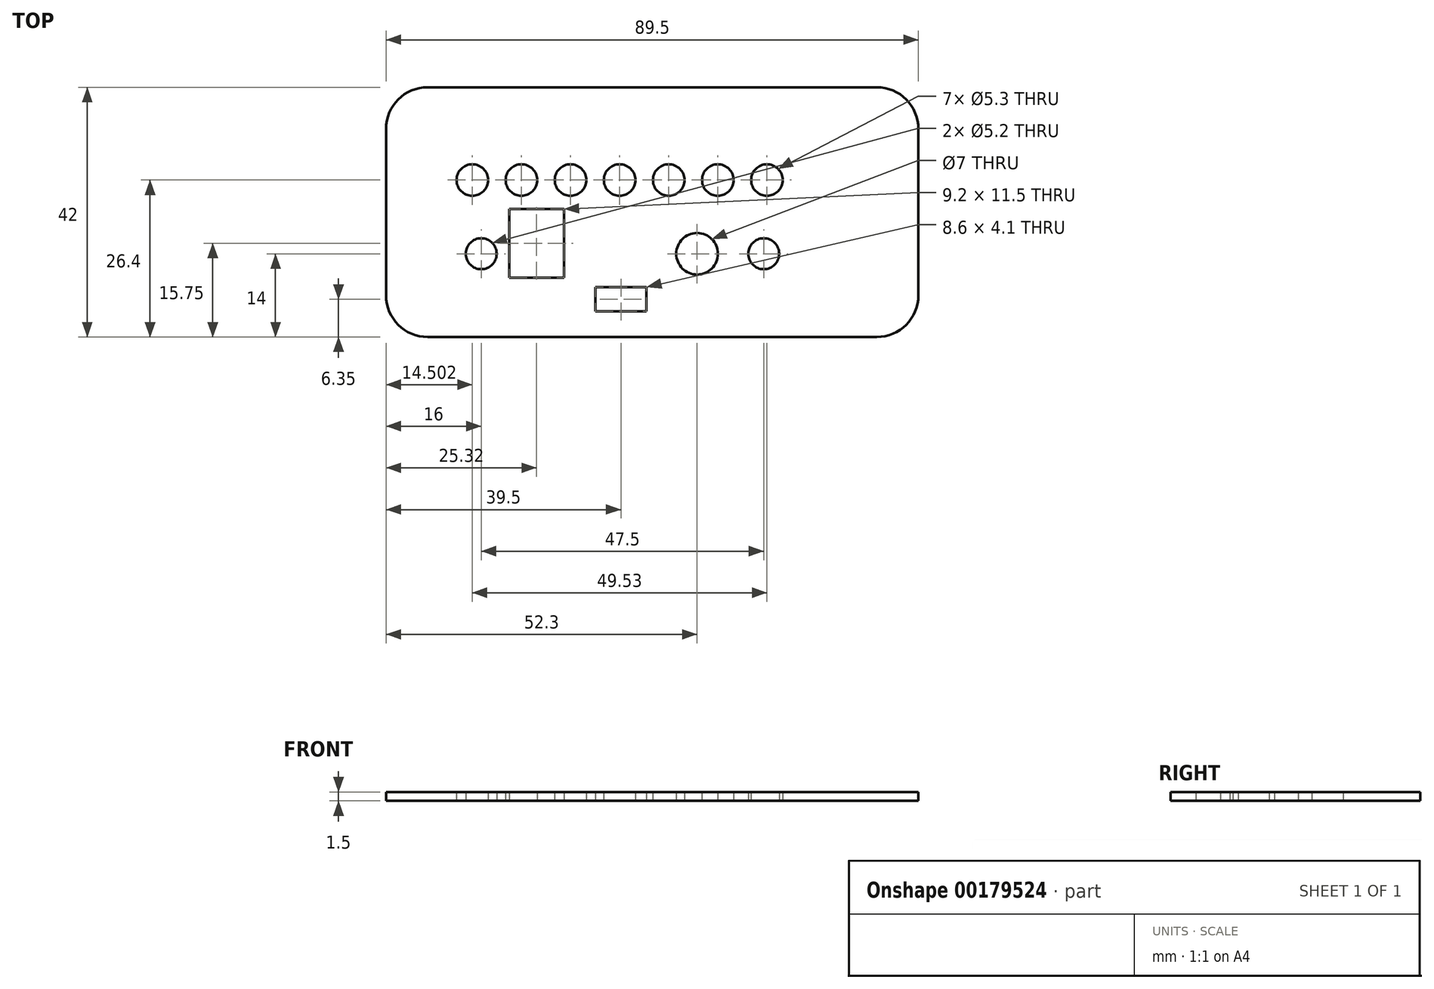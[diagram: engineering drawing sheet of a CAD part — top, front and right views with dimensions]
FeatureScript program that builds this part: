
annotation { "Feature Type Name" : "Feature", "Feature Type Description" : "" }
export const myFeature = defineFeature(function(context is Context, id is Id, definition is map)
    precondition{}
    {
        {
            var Q0;
            Q0=qCreatedBy(makeId("Top.planeOp"),FACE);
            var sketch = newSketch(context, id + "F0", { "sketchPlane" : qUnion([Q0])});
            skLineSegment(sketch, "E0.bottom", {"start": v(37.75, -21) * mm, "end": v(-37.75, -21) * mm});
            skLineSegment(sketch, "E0.top", {"start": v(37.75, 21) * mm, "end": v(-37.75, 21) * mm});
            skLineSegment(sketch, "E0.left", {"start": v(44.75, -14) * mm, "end": v(44.75, 14) * mm});
            skLineSegment(sketch, "E0.right", {"start": v(-44.75, -14) * mm, "end": v(-44.75, 14) * mm});
            skPoint(sketch, "E0.middle", {"position": v(0, 0) * mm});
            skPoint(sketch, "E1.visualSharp", {"position": v(-44.75, 21) * mm});
            skArc(sketch, "E1.filletArc", {"start": v(-37.75, 21) * mm, "mid": v(-42.7, 18.95) * mm, "end": v(-44.75, 14) * mm});
            skPoint(sketch, "E2.visualSharp", {"position": v(-44.75, -21) * mm});
            skArc(sketch, "E2.filletArc", {"start": v(-44.75, -14) * mm, "mid": v(-42.7, -18.95) * mm, "end": v(-37.75, -21) * mm});
            skPoint(sketch, "E3.visualSharp", {"position": v(44.75, 21) * mm});
            skArc(sketch, "E3.filletArc", {"start": v(44.75, 14) * mm, "mid": v(42.7, 18.95) * mm, "end": v(37.75, 21) * mm});
            skPoint(sketch, "E4.visualSharp", {"position": v(44.75, -21) * mm});
            skArc(sketch, "E4.filletArc", {"start": v(37.75, -21) * mm, "mid": v(42.7, -18.95) * mm, "end": v(44.75, -14) * mm});
            skLineSegment(sketch, "E5.bottom", {"start": v(-9.55, -12.6) * mm, "end": v(-0.95, -12.6) * mm});
            skLineSegment(sketch, "E5.top", {"start": v(-9.55, -16.7) * mm, "end": v(-0.95, -16.7) * mm});
            skLineSegment(sketch, "E5.left", {"start": v(-9.55, -12.6) * mm, "end": v(-9.55, -16.7) * mm});
            skLineSegment(sketch, "E5.right", {"start": v(-0.95, -12.6) * mm, "end": v(-0.95, -16.7) * mm});
            skPoint(sketch, "E6", {"position": v(7.55, -7) * mm});
            skPoint(sketch, "E7", {"position": v(18.75, -7) * mm});
            skPoint(sketch, "E8", {"position": v(-28.75, -7) * mm});
            skLineSegment(sketch, "E9.bottom", {"start": v(-24.03, 0.5) * mm, "end": v(-14.83, 0.5) * mm});
            skLineSegment(sketch, "E9.top", {"start": v(-24.03, -11) * mm, "end": v(-14.83, -11) * mm});
            skLineSegment(sketch, "E9.left", {"start": v(-24.03, 0.5) * mm, "end": v(-24.03, -11) * mm});
            skLineSegment(sketch, "E9.right", {"start": v(-14.83, 0.5) * mm, "end": v(-14.83, -11) * mm});
            skPoint(sketch, "E10", {"position": v(-30.25, 5.4) * mm});
            skPoint(sketch, "E11.1.0.0", {"position": v(-22, 5.4) * mm});
            skPoint(sketch, "E11.2.0.0", {"position": v(-13.74, 5.4) * mm});
            skPoint(sketch, "E11.3.0.0", {"position": v(-5.48, 5.4) * mm});
            skPoint(sketch, "E11.4.0.0", {"position": v(2.77, 5.4) * mm});
            skPoint(sketch, "E11.5.0.0", {"position": v(11.03, 5.4) * mm});
            skPoint(sketch, "E11.6.0.0", {"position": v(19.28, 5.4) * mm});
            skLineSegment(sketch, "E11.direction1", {"start": v(-30.25, 5.4) * mm, "end": v(-22, 5.4) * mm, "construction": true});
            skLineSegment(sketch, "E11.direction2", {"start": v(-30.25, 5.4) * mm, "end": v(-30.25, 15.4) * mm, "construction": true});
            skSolve(sketch);
        }
        {
            var Q0;
            Q0=makeQuery(id+"F0.imprint","IMPRINT",FACE,{"disambiguationData":[TD([[makeQuery(id+"F0.imprint","IMPRINT",EDGE,{"derivedFrom":sQuery(id+"F0.wireOp",EDGE,"E0.bottom")}),-1.0]])]});
            extrude(context, id + "F1", {"entities" : qUnion([Q0]), "depth" : 1.5 * mm});
        }
        {
            var Q0;
            Q0=sQuery(id+"F0.wireOp",VERTEX,"E7");
            var Q1;
            Q1=sQuery(id+"F0.wireOp",VERTEX,"E8");
            var Q2;
            Q2=makeQuery(id+"F1.opExtrude","SWEPT_BODY",BODY,{"disambiguationData":[OSD([sQuery(id+"F0.wireOp",EDGE,"E0.bottom"),sQuery(id+"F0.wireOp",EDGE,"E0.top"),sQuery(id+"F0.wireOp",EDGE,"E0.left"),sQuery(id+"F0.wireOp",EDGE,"E0.right"),sQuery(id+"F0.wireOp",EDGE,"E1.filletArc"),sQuery(id+"F0.wireOp",EDGE,"E2.filletArc"),sQuery(id+"F0.wireOp",EDGE,"E3.filletArc"),sQuery(id+"F0.wireOp",EDGE,"E4.filletArc"),sQuery(id+"F0.wireOp",EDGE,"E5.bottom"),sQuery(id+"F0.wireOp",EDGE,"E5.top"),sQuery(id+"F0.wireOp",EDGE,"E5.left"),sQuery(id+"F0.wireOp",EDGE,"E5.right"),sQuery(id+"F0.wireOp",EDGE,"E9.bottom"),sQuery(id+"F0.wireOp",EDGE,"E9.top"),sQuery(id+"F0.wireOp",EDGE,"E9.left"),sQuery(id+"F0.wireOp",EDGE,"E9.right")])]});
            hole(context, id + "F2", {"style" : HoleStyle.SIMPLE, "endStyle" : HoleEndStyle.BLIND, "oppositeDirection" : true, "holeDiameter" : 5.2 * mm, "holeDepth" : 2 * mm, "locations" : qUnion([Q0, Q1]), "scope" : qUnion([Q2])});
        }
        {
            var Q0;
            Q0=sQuery(id+"F0.wireOp",VERTEX,"E6");
            var Q1;
            Q1=makeQuery(id+"F1.opExtrude","SWEPT_BODY",BODY,{"disambiguationData":[OSD([sQuery(id+"F0.wireOp",EDGE,"E0.bottom"),sQuery(id+"F0.wireOp",EDGE,"E0.top"),sQuery(id+"F0.wireOp",EDGE,"E0.left"),sQuery(id+"F0.wireOp",EDGE,"E0.right"),sQuery(id+"F0.wireOp",EDGE,"E1.filletArc"),sQuery(id+"F0.wireOp",EDGE,"E2.filletArc"),sQuery(id+"F0.wireOp",EDGE,"E3.filletArc"),sQuery(id+"F0.wireOp",EDGE,"E4.filletArc"),sQuery(id+"F0.wireOp",EDGE,"E5.bottom"),sQuery(id+"F0.wireOp",EDGE,"E5.top"),sQuery(id+"F0.wireOp",EDGE,"E5.left"),sQuery(id+"F0.wireOp",EDGE,"E5.right"),sQuery(id+"F0.wireOp",EDGE,"E9.bottom"),sQuery(id+"F0.wireOp",EDGE,"E9.top"),sQuery(id+"F0.wireOp",EDGE,"E9.left"),sQuery(id+"F0.wireOp",EDGE,"E9.right")])]});
            hole(context, id + "F3", {"style" : HoleStyle.SIMPLE, "endStyle" : HoleEndStyle.BLIND, "oppositeDirection" : true, "holeDiameter" : 7 * mm, "holeDepth" : 2 * mm, "locations" : qUnion([Q0]), "scope" : qUnion([Q1])});
        }
        {
            var Q0;
            Q0=sQuery(id+"F0.wireOp",VERTEX,"E10");
            var Q1;
            Q1=sQuery(id+"F0.wireOp",VERTEX,"E11.0.1.0");
            var Q2;
            Q2=sQuery(id+"F0.wireOp",VERTEX,"E11.1.1.0");
            var Q3;
            Q3=sQuery(id+"F0.wireOp",VERTEX,"E11.1.0.0");
            var Q4;
            Q4=sQuery(id+"F0.wireOp",VERTEX,"E11.2.1.0");
            var Q5;
            Q5=sQuery(id+"F0.wireOp",VERTEX,"E11.2.0.0");
            var Q6;
            Q6=sQuery(id+"F0.wireOp",VERTEX,"E11.3.1.0");
            var Q7;
            Q7=sQuery(id+"F0.wireOp",VERTEX,"E11.3.0.0");
            var Q8;
            Q8=sQuery(id+"F0.wireOp",VERTEX,"E11.4.1.0");
            var Q9;
            Q9=sQuery(id+"F0.wireOp",VERTEX,"E11.4.0.0");
            var Q10;
            Q10=sQuery(id+"F0.wireOp",VERTEX,"E11.5.1.0");
            var Q11;
            Q11=sQuery(id+"F0.wireOp",VERTEX,"E11.5.0.0");
            var Q12;
            Q12=sQuery(id+"F0.wireOp",VERTEX,"E11.6.1.0");
            var Q13;
            Q13=sQuery(id+"F0.wireOp",VERTEX,"E11.6.0.0");
            var Q14;
            Q14=makeQuery(id+"F1.opExtrude","SWEPT_BODY",BODY,{"disambiguationData":[OSD([sQuery(id+"F0.wireOp",EDGE,"E0.bottom"),sQuery(id+"F0.wireOp",EDGE,"E0.top"),sQuery(id+"F0.wireOp",EDGE,"E0.left"),sQuery(id+"F0.wireOp",EDGE,"E0.right"),sQuery(id+"F0.wireOp",EDGE,"E1.filletArc"),sQuery(id+"F0.wireOp",EDGE,"E2.filletArc"),sQuery(id+"F0.wireOp",EDGE,"E3.filletArc"),sQuery(id+"F0.wireOp",EDGE,"E4.filletArc"),sQuery(id+"F0.wireOp",EDGE,"E5.bottom"),sQuery(id+"F0.wireOp",EDGE,"E5.top"),sQuery(id+"F0.wireOp",EDGE,"E5.left"),sQuery(id+"F0.wireOp",EDGE,"E5.right"),sQuery(id+"F0.wireOp",EDGE,"E9.bottom"),sQuery(id+"F0.wireOp",EDGE,"E9.top"),sQuery(id+"F0.wireOp",EDGE,"E9.left"),sQuery(id+"F0.wireOp",EDGE,"E9.right")])]});
            hole(context, id + "F4", {"style" : HoleStyle.SIMPLE, "endStyle" : HoleEndStyle.BLIND, "oppositeDirection" : true, "holeDiameter" : 5.3 * mm, "holeDepth" : 2 * mm, "locations" : qUnion([Q0, Q1, Q2, Q3, Q4, Q5, Q6, Q7, Q8, Q9, Q10, Q11, Q12, Q13]), "scope" : qUnion([Q14])});
        }
    });
